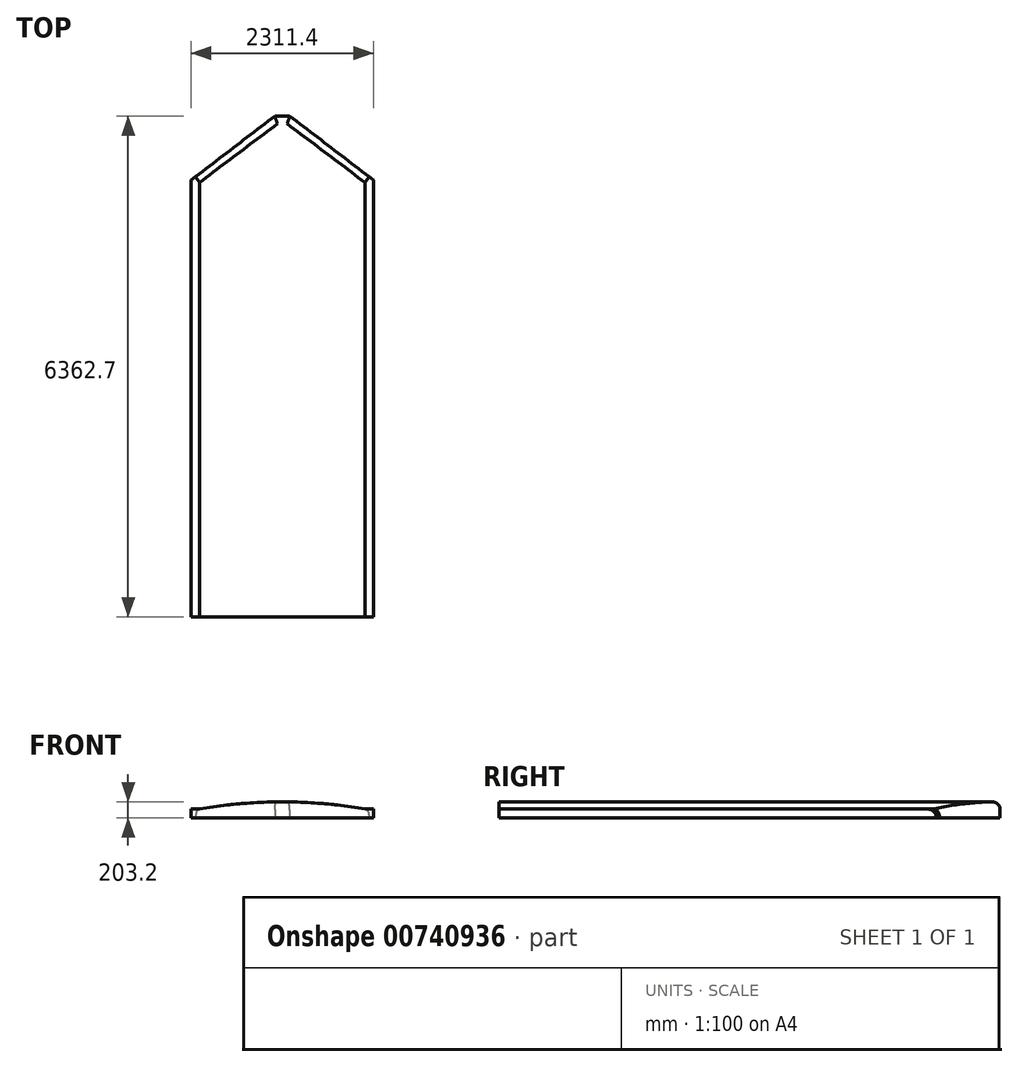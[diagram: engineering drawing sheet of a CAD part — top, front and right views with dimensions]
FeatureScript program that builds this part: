
annotation { "Feature Type Name" : "Feature", "Feature Type Description" : "" }
export const myFeature = defineFeature(function(context is Context, id is Id, definition is map)
    precondition{}
    {
        {
            var Q0;
            Q0=qCreatedBy(makeId("Top.planeOp"),FACE);
            var sketch = newSketch(context, id + "F0", { "sketchPlane" : qUnion([Q0])});
            skLineSegment(sketch, "E0.bottom", {"start": v(-1228.2, -3819.59) * mm, "end": v(1159.4, -3819.59) * mm});
            skLineSegment(sketch, "E0.left", {"start": v(-1228.2, -3819.59) * mm, "end": v(-1228.2, 1705.71) * mm});
            skLineSegment(sketch, "E0.right", {"start": v(1159.4, -3819.59) * mm, "end": v(1159.4, 1705.71) * mm});
            skLineSegment(sketch, "E1", {"start": v(-1178.43, 1806.53) * mm, "end": v(-34.4, 2682.81) * mm});
            skLineSegment(sketch, "E2", {"start": v(-34.4, 2682.81) * mm, "end": v(1109.62, 1806.53) * mm});
            skLineSegment(sketch, "E3", {"start": v(-1228.2, 1768.41) * mm, "end": v(1159.4, 1768.41) * mm, "construction": true});
            skPoint(sketch, "E4", {"position": v(-34.4, 1768.41) * mm});
            skLineSegment(sketch, "E5", {"start": v(-34.4, 3603.46) * mm, "end": v(-34.4, -5272.56) * mm, "construction": true});
            skPoint(sketch, "E6.visualSharp", {"position": v(-1228.2, 1768.41) * mm});
            skArc(sketch, "E6.filletArc", {"start": v(-1178.43, 1806.53) * mm, "mid": v(-1215.08, 1761.93) * mm, "end": v(-1228.2, 1705.71) * mm});
            skPoint(sketch, "E7.visualSharp", {"position": v(1159.4, 1768.41) * mm});
            skArc(sketch, "E7.filletArc", {"start": v(1159.4, 1705.71) * mm, "mid": v(1146.27, 1761.93) * mm, "end": v(1109.62, 1806.53) * mm});
            skLineSegment(sketch, "E8.bottom", {"start": v(-1190.1, 1768.41) * mm, "end": v(1121.3, 1768.41) * mm, "construction": true});
            skLineSegment(sketch, "E8.top", {"start": v(-1190.1, -3781.49) * mm, "end": v(1121.3, -3781.49) * mm});
            skLineSegment(sketch, "E8.left", {"start": v(-1190.1, 1768.41) * mm, "end": v(-1190.1, -3781.49) * mm});
            skLineSegment(sketch, "E8.right", {"start": v(1121.3, 1768.41) * mm, "end": v(1121.3, -3781.49) * mm});
            skLineSegment(sketch, "E9", {"start": v(-1190.1, 1768.41) * mm, "end": v(-128.95, 2581.21) * mm});
            skLineSegment(sketch, "E10", {"start": v(-128.95, 2581.21) * mm, "end": v(60.14, 2581.21) * mm});
            skLineSegment(sketch, "E11", {"start": v(60.14, 2581.21) * mm, "end": v(1121.3, 1768.41) * mm});
            skLineSegment(sketch, "E12", {"start": v(1159.4, -3781.49) * mm, "end": v(1121.3, -3781.49) * mm, "construction": true});
            skLineSegment(sketch, "E13", {"start": v(-1228.2, -3781.49) * mm, "end": v(-1190.1, -3781.49) * mm, "construction": true});
            skLineSegment(sketch, "E14", {"start": v(1121.3, -3781.49) * mm, "end": v(1121.3, -3819.59) * mm});
            skSolve(sketch);
        }
        {
            var Q0;
            Q0=makeQuery(id+"F0.imprint","IMPRINT",FACE,{"disambiguationData":[TD([[makeQuery(id+"F0.imprint","IMPRINT",EDGE,{"derivedFrom":sQuery(id+"F0.wireOp",EDGE,"E8.top")}),1.0]])]});
            extrude(context, id + "F1", {"entities" : qUnion([Q0]), "depth" : 203.2 * mm, "offsetDistance" : 25.4 * mm});
        }
        {
            var Q0;
            Q0=makeQuery(id+"F1.opExtrude","SWEPT_FACE",FACE,{"disambiguationData":[OSD([sQuery(id+"F0.wireOp",EDGE,"E8.top")])]});
            var sketch = newSketch(context, id + "F2", { "sketchPlane" : qUnion([Q0])});
            skPoint(sketch, "E15", {"position": v(-34.4, 203.2) * mm});
            skArc(sketch, "E16", {"start": v(1013.34, 114.3) * mm, "mid": v(-34.4, 203.2) * mm, "end": v(-1082.16, 114.3) * mm});
            skLineSegment(sketch, "E17", {"start": v(1013.34, 114.3) * mm, "end": v(1121.3, 114.3) * mm});
            skLineSegment(sketch, "E18", {"start": v(-1082.16, 114.3) * mm, "end": v(-1190.1, 114.3) * mm});
            skLineSegment(sketch, "E19", {"start": v(-1190.1, 114.3) * mm, "end": v(-1190.1, 203.2) * mm});
            skLineSegment(sketch, "E20", {"start": v(-1190.1, 203.2) * mm, "end": v(1121.3, 203.2) * mm});
            skLineSegment(sketch, "E21", {"start": v(1121.3, 203.2) * mm, "end": v(1121.3, 114.3) * mm});
            skSolve(sketch);
        }
        {
            var Q0;
            {var subQ0=sQuery(id+"F2.wireOp",EDGE,"E17");Q0=makeQuery(id+"F2.imprint","IMPRINT",FACE,{"disambiguationData":[TD([[makeQuery(id+"F2.imprint","IMPRINT",EDGE,{"derivedFrom":subQ0}),1.0]])]});}
            var Q1;
            {var subQ0=sQuery(id+"F2.wireOp",EDGE,"E18");Q1=makeQuery(id+"F2.imprint","IMPRINT",FACE,{"disambiguationData":[TD([[makeQuery(id+"F2.imprint","IMPRINT",EDGE,{"derivedFrom":subQ0}),-1.0]])]});}
            extrude(context, id + "F3", {"entities" : qUnion([Q0, Q1]), "operationType" : NewBodyOperationType.REMOVE, "oppositeDirection" : true, "depth" : 6451.6 * mm, "offsetDistance" : 25.4 * mm});
        }
        {
            var Q0;
            Q0=makeQuery(id+"F3.boolean.opBoolean","COPY",EDGE,{"derivedFrom":makeQuery(id+"F3.opExtrude","SWEPT_EDGE",EDGE,{"disambiguationData":[OSD([sQuery(id+"F0.wireOp",EDGE,"E8.top"),sQuery(id+"F0.wireOp",EDGE,"E8.right"),sQuery(id+"F2.wireOp",EDGE,"E17"),sQuery(id+"F2.wireOp",EDGE,"E21")])]})});
            var Q1;
            {var subQ0=sQuery(id+"F2.wireOp",EDGE,"E16");Q1=makeQuery(id+"F3.boolean.opBoolean","INTERSECT",EDGE,{"derivedFrom":[makeQuery(id+"F1.opExtrude","SWEPT_FACE",FACE,{"disambiguationData":[OSD([sQuery(id+"F0.wireOp",EDGE,"E11")])]}),makeQuery(id+"F3.opExtrude","SWEPT_FACE",FACE,{"disambiguationData":[OSD([subQ0]),TDD([makeQuery(id+"F2.imprint","IMPRINT",EDGE,{"disambiguationData":[TD([[makeQuery(id+"F2.imprint","INTERSECT",VERTEX,{"derivedFrom":[subQ0,sQuery(id+"F2.wireOp",EDGE,"E17")]}),-1.0]])],"derivedFrom":subQ0})])]})]});}
            var Q2;
            {var subQ0=sQuery(id+"F2.wireOp",EDGE,"E16");Q2=makeQuery(id+"F3.boolean.opBoolean","INTERSECT",EDGE,{"derivedFrom":[makeQuery(id+"F1.opExtrude","SWEPT_FACE",FACE,{"disambiguationData":[OSD([sQuery(id+"F0.wireOp",EDGE,"E9")])]}),makeQuery(id+"F3.opExtrude","SWEPT_FACE",FACE,{"disambiguationData":[OSD([subQ0]),TDD([makeQuery(id+"F2.imprint","IMPRINT",EDGE,{"disambiguationData":[TD([[makeQuery(id+"F2.imprint","INTERSECT",VERTEX,{"derivedFrom":[subQ0,sQuery(id+"F2.wireOp",EDGE,"E17")]}),-1.0]])],"derivedFrom":subQ0})])]}),makeQuery(id+"F3.opExtrude","SWEPT_FACE",FACE,{"disambiguationData":[OSD([subQ0]),TDD([makeQuery(id+"F2.imprint","IMPRINT",EDGE,{"disambiguationData":[TD([[makeQuery(id+"F2.imprint","INTERSECT",VERTEX,{"derivedFrom":[subQ0,sQuery(id+"F2.wireOp",EDGE,"E18")]}),1.0]])],"derivedFrom":subQ0})])]})]});}
            var Q3;
            Q3=makeQuery(id+"F3.boolean.opBoolean","INTERSECT",EDGE,{"derivedFrom":[makeQuery(id+"F1.opExtrude","SWEPT_FACE",FACE,{"disambiguationData":[OSD([sQuery(id+"F0.wireOp",EDGE,"E11")])]}),makeQuery(id+"F3.opExtrude","SWEPT_FACE",FACE,{"disambiguationData":[OSD([sQuery(id+"F2.wireOp",EDGE,"E17")])]})]});
            var Q4;
            Q4=makeQuery(id+"F3.boolean.opBoolean","INTERSECT",EDGE,{"derivedFrom":[makeQuery(id+"F1.opExtrude","SWEPT_FACE",FACE,{"disambiguationData":[OSD([sQuery(id+"F0.wireOp",EDGE,"E9")])]}),makeQuery(id+"F3.opExtrude","SWEPT_FACE",FACE,{"disambiguationData":[OSD([sQuery(id+"F2.wireOp",EDGE,"E18")])]})]});
            var Q5;
            Q5=makeQuery(id+"F3.boolean.opBoolean","COPY",EDGE,{"derivedFrom":makeQuery(id+"F3.opExtrude","SWEPT_EDGE",EDGE,{"disambiguationData":[OSD([sQuery(id+"F0.wireOp",EDGE,"E8.top"),sQuery(id+"F0.wireOp",EDGE,"E8.left"),sQuery(id+"F2.wireOp",EDGE,"E18"),sQuery(id+"F2.wireOp",EDGE,"E19")])]})});
            var Q6;
            {var subQ0=sQuery(id+"F2.wireOp",EDGE,"E16");Q6=makeQuery(id+"F3.boolean.opBoolean","INTERSECT",EDGE,{"derivedFrom":[makeQuery(id+"F1.opExtrude","SWEPT_FACE",FACE,{"disambiguationData":[OSD([sQuery(id+"F0.wireOp",EDGE,"E10")])]}),makeQuery(id+"F3.opExtrude","SWEPT_FACE",FACE,{"disambiguationData":[OSD([subQ0]),TDD([makeQuery(id+"F2.imprint","IMPRINT",EDGE,{"disambiguationData":[TD([[makeQuery(id+"F2.imprint","INTERSECT",VERTEX,{"derivedFrom":[subQ0,sQuery(id+"F2.wireOp",EDGE,"E17")]}),-1.0]])],"derivedFrom":subQ0})])]}),makeQuery(id+"F3.opExtrude","SWEPT_FACE",FACE,{"disambiguationData":[OSD([subQ0]),TDD([makeQuery(id+"F2.imprint","IMPRINT",EDGE,{"disambiguationData":[TD([[makeQuery(id+"F2.imprint","INTERSECT",VERTEX,{"derivedFrom":[subQ0,sQuery(id+"F2.wireOp",EDGE,"E18")]}),1.0]])],"derivedFrom":subQ0})])]})]});}
            fillet(context, id + "F4", {"entities" : qUnion([Q0, Q1, Q2, Q3, Q4, Q5, Q6]), "radius" : 98.42 * mm, "tangentPropagation" : true, "allowEdgeOverflow" : false});
        }
    });
